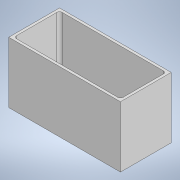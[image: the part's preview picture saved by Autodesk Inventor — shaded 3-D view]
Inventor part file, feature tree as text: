
AUTODESK INVENTOR PART (.ipt)
format: ipt  version: 2020 (Build 240168000, 168)  size: 110,080 bytes
history: native  units: mm
features: extrude x2, sketch x2
ambient origin geometry x8: Origin, YZ Plane, XZ Plane, XY Plane, X Axis, Y Axis, Z Axis, Center Point
bodies: Solid1 (feature_tree)
feature tree (4):
  extrude  "Extrusion1"  Depth=100.0mm
  extrude  "Extrusion2"  Depth=5.0mm
  sketch  "Sketch1"  dims[d0=220.0mm d1=100.0mm]
  sketch  "Sketch2"  dims[d2=120.0mm d3=0.0mm d4=5.0mm d5=5.0mm d6=5.0mm d7=5.0mm d8=5.0mm d9=115.0mm d10=0.0mm]
